# Revit family: Shower-Showerhead-KOHLER-Contemporary-K-99945T
name_source: partatom
category: Plumbing Fixtures
units: mm (PartAtom-declared; Revit-internal decimal feet)

## family parameters
Cut with Voids When Loaded = No
Host = Face
OmniClass Number = 23.31.17.00
OmniClass Title = Showers
Part Type = Normal
Room Calculation Point = No
Round Connector Dimension = Use Diameter
Shared = No

## types (4) — shared parameters
ADA Compliant = No
Assembly Code = D2010700
CW Connection = No
Cold Water Inlet = Cold Water Inlet
Date Modified = 01/10/2025
Default Elevation = 0"
Description = 8inch Round Rain Overhead - Plastic Modern
Drain Included = No
Flow Rate = 0 GPM
HW Connection = Yes
Height = 2 7/16"
Hot Water Inlet = Hot Water Inlet
Length = 8"
Manufacturer = Kohler Co.
Master Format 2014 = 22 42 23
Master Format 2014 Name = Residential Showers
Material = Brass Construction
Pressure = 0.00 psi
Product Name = Contemporary
Tempered Water Inlet = Tempered Water Inlet
URL = http://www.kohler.com.cn
Vent Connection = No
Waste Connection = No
Waste Water Outlet = Waste Water Outlet
WaterSense Certified = No
Width = 8"

## per-type parameters (varying)
| type | Finish | Model | Product Documentation Link | Product Page URL | Type |
| Without Katalyst Air Induction Technology , CP-Polished Chrome | Kohler-Metal-CP-Polished_Chrome | K-99945T-CL-CP | https://files.kohler.com.cn |  | 1 |
| With Katalyst Air Induction Technology , CP-Polished Chrome | Kohler-Metal-CP-Polished_Chrome | K-99945T-E-CP |  |  | 2 |
| Without Katalyst Air Induction Technology , BL-Matte Black | Kohler-Metal-BL-Matte_Black | K-99945T-CL-BL | https://files.kohler.com.cn |  | 3 |
| Without Katalyst Air Induction Technology ,LBN-Non Pvd Brushed Nickel | Kohler-Metal-LBN-Non_Pvd_Brushed_Nickel | K-99945T-CL-LBN | https://files.kohler.com.cn | https://www.kohler.com.cn | 4 |

## geometry (parser evidence)
native form markers: Sweep x5
no freeform markers — native parametric forms only
